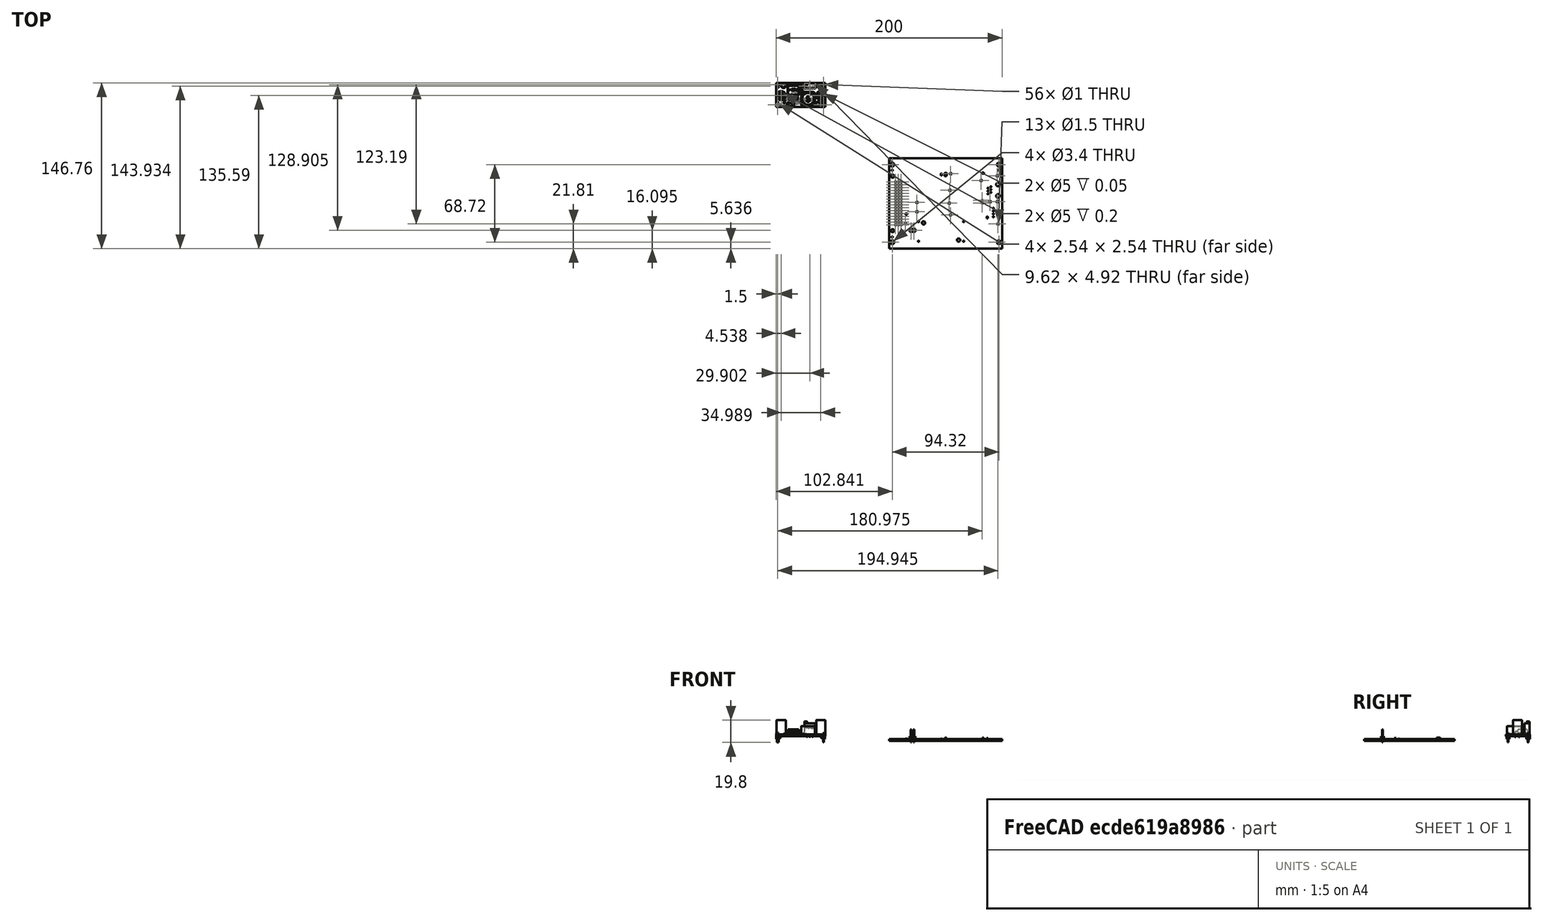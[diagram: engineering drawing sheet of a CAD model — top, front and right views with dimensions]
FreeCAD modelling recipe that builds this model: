
FCSTD DOCUMENT  (FreeCAD 0.19R24291 (Git))
Label: PolyVent_SPI_Controller_FreeCAD
License: All rights reserved
LicenseURL: http://en.wikipedia.org/wiki/All_rights_reserved
objects: Part::Feature×93, App::Link×56, App::Part×6, PartDesign::CoordinateSystem×1, Sketcher::SketchObject×1
note: 95 computed .brp shape members not serialized (recipe doc carries the construction recipe); baked Part::Feature solids carry a one-line shape summary decoded from their .brp

FEATURE [PartDesign::CoordinateSystem] Local_CS_b92b
  AttacherType = Attacher::AttachEngine3D
FEATURE [Part::Feature] Pcb_b92b
  shape: bbox 100 x 80 x 1.6 mm, 103 faces (baked)
FEATURE [Sketcher::SketchObject] PCB_Sketch_b92b
  FullyConstrained = false
  sketch-geometry (4):
    g0: LineSegment StartX=198.501 StartY=-145.004 StartZ=0 EndX=198.501 EndY=-65.0036 EndZ=0
    g1: LineSegment StartX=98.5011 StartY=-65.0036 StartZ=0 EndX=98.5011 EndY=-145.004 EndZ=0
    g2: LineSegment StartX=98.5011 StartY=-145.004 StartZ=0 EndX=198.501 EndY=-145.004 EndZ=0
    g3: LineSegment StartX=198.501 StartY=-65.0036 StartZ=0 EndX=98.5011 EndY=-65.0036 EndZ=0
  constraints (4):
    c: Coincident(g1,g2)
    c: Coincident(g1,g3)
    c: Coincident(g0,g2)
    c: Coincident(g0,g3)
FEATURE [App::Part] Board_Geoms_b92b
  Group = -> [Local_CS_b92b,Pcb_b92b,PCB_Sketch_b92b]
  Origin = -> Origin
FEATURE [Part::Feature] Shape  label="R113_R_0603_1608Metric_375481a100d2"
  Placement = pos=(144.78,-79.375,0) rot=(0,0,-1;1.5708rad)
  shape: bbox 0.8 x 1.6 x 0.45 mm, 26 faces (baked)
FEATURE [Part::Feature] Shape001  label="F103_Fuse_0603_1608Metric_acc948c9a6c3"
  Placement = pos=(113.817,-114.3,0) rot=(0,0,1;0rad)
  shape: bbox 1.6 x 0.8 x 0.45 mm, 26 faces (baked)
FEATURE [Part::Feature] Part__Feature  label="TestPoint_Loop_D2_54mm_Drill1_5mm_Beaded_cp"
  shape: bbox 3 x 3 x 3 mm, 4 faces (baked)
FEATURE [Part::Feature] Part__Feature001  label="TestPoint_Loop_D2_54mm_Drill1_5mm_Beaded_cp001"
  shape: bbox 3.415 x 0.9501 x 9.255 mm, 7 faces (baked)
FEATURE [App::Part] TestPoint_Loop_D2_54mm_Drill1_5mm_Beaded_cp  label="TP101_TestPoint_Loop_D2_54mm_Drill1_5mm_Beaded_cp002_d4c60d019c71"
  Group = -> [Part__Feature,Part__Feature001]
  Origin = -> Origin008
  Placement = pos=(180,-84.7725,0) rot=(0,0,1;0rad)
FEATURE [App::Link] R113_R_0603_1608Metric_375481a100d2_ln_  label="R107_R_0603_1608Metric_76be1ec9b680"
  LinkPlacement = pos=(147.678,-118.11,0) rot=(0,0,1;3.14159rad)
  LinkedObject = -> Shape
  Placement = pos=(147.678,-118.11,0) rot=(0,0,1;3.14159rad)
FEATURE [App::Link] R113_R_0603_1608Metric_375481a100d2_ln_001  label="R205_R_0603_1608Metric_6ebf565c5914"
  LinkPlacement = pos=(182.626,-111.76,0) rot=(0,0,1;3.14159rad)
  LinkedObject = -> Shape
  Placement = pos=(182.626,-111.76,0) rot=(0,0,1;3.14159rad)
FEATURE [App::Link] TP101_TestPoint_Loop_D2_54mm_Drill1_5mm_Beaded_cp002_d4c60d019c71_ln_  label="TP103_TestPoint_Loop_D2_54mm_Drill1_5mm_Beaded_cp002_1430d18448d9"
  LinkPlacement = pos=(152.4,-93.345,0) rot=(0,0,1;0rad)
  LinkedObject = -> TestPoint_Loop_D2_54mm_Drill1_5mm_Beaded_cp
  Placement = pos=(152.4,-93.345,0) rot=(0,0,1;0rad)
FEATURE [Part::Feature] Shape002  label="D101_LED_0603_1608Metric_bc9d04248380"
  Placement = pos=(181.61,-78.105,0) rot=(0,0,1;3.14159rad)
  shape: bbox 1.6 x 0.8 x 1.1 mm, 50 faces (baked)
FEATURE [App::Link] R113_R_0603_1608Metric_375481a100d2_ln_002  label="R102_R_0603_1608Metric_2d86cc6ea8c2"
  LinkPlacement = pos=(119.38,-133.35,0) rot=(0,0,1;0rad)
  LinkedObject = -> Shape
  Placement = pos=(119.38,-133.35,0) rot=(0,0,1;0rad)
FEATURE [App::Link] R113_R_0603_1608Metric_375481a100d2_ln_003  label="R111_R_0603_1608Metric_b8d57b534feb"
  LinkPlacement = pos=(144.145,-83.185,0) rot=(0,0,1;0rad)
  LinkedObject = -> Shape
  Placement = pos=(144.145,-83.185,0) rot=(0,0,1;0rad)
FEATURE [App::Link] R113_R_0603_1608Metric_375481a100d2_ln_004  label="R105_R_0603_1608Metric_261db71a386c"
  LinkPlacement = pos=(146.685,-109.22,0) rot=(0,0,1;3.14159rad)
  LinkedObject = -> Shape
  Placement = pos=(146.685,-109.22,0) rot=(0,0,1;3.14159rad)
FEATURE [App::Link] R113_R_0603_1608Metric_375481a100d2_ln_005  label="R117_R_0603_1608Metric_bc3712dd90b9"
  LinkPlacement = pos=(177.165,-78.105,0) rot=(0,0,1;3.14159rad)
  LinkedObject = -> Shape
  Placement = pos=(177.165,-78.105,0) rot=(0,0,1;3.14159rad)
FEATURE [App::Link] TP101_TestPoint_Loop_D2_54mm_Drill1_5mm_Beaded_cp002_d4c60d019c71_ln_001  label="TP106_TestPoint_Loop_D2_54mm_Drill1_5mm_Beaded_cp002_896a11763af9"
  LinkPlacement = pos=(123.19,-104.14,0) rot=(0,0,1;0rad)
  LinkedObject = -> TestPoint_Loop_D2_54mm_Drill1_5mm_Beaded_cp
  Placement = pos=(123.19,-104.14,0) rot=(0,0,1;0rad)
FEATURE [Part::Feature] Shape003  label="C202_C_0603_1608Metric_93a6a18d32bc"
  Placement = pos=(185.42,-117.475,0) rot=(0,0,-1;1.5708rad)
  shape: bbox 0.8 x 1.6 x 0.8 mm, 28 faces (baked)
FEATURE [App::Link] R113_R_0603_1608Metric_375481a100d2_ln_006  label="R108_R_0603_1608Metric_d8c6bf93a453"
  LinkPlacement = pos=(153.67,-83.185,0) rot=(0,0,1;3.14159rad)
  LinkedObject = -> Shape
  Placement = pos=(153.67,-83.185,0) rot=(0,0,1;3.14159rad)
FEATURE [App::Link] TP101_TestPoint_Loop_D2_54mm_Drill1_5mm_Beaded_cp002_d4c60d019c71_ln_002  label="TP203_TestPoint_Loop_D2_54mm_Drill1_5mm_Beaded_cp002_adb0e327fc1a"
  LinkPlacement = pos=(194.945,-123.19,0) rot=(0,0,1;0rad)
  LinkedObject = -> TestPoint_Loop_D2_54mm_Drill1_5mm_Beaded_cp
  Placement = pos=(194.945,-123.19,0) rot=(0,0,1;0rad)
FEATURE [App::Link] R113_R_0603_1608Metric_375481a100d2_ln_007  label="R103_R_0603_1608Metric_aa3dbe28ece3"
  LinkPlacement = pos=(148.59,-83.185,0) rot=(0,0,1;3.14159rad)
  LinkedObject = -> Shape
  Placement = pos=(148.59,-83.185,0) rot=(0,0,1;3.14159rad)
FEATURE [Part::Feature] Shape004  label="Q102_SOT_23_961175d790bb"
  Placement = pos=(148.59,-79.375,0) rot=(0,0,1;0rad)
  shape: bbox 2.5 x 3 x 1.2 mm, 76 faces (baked)
FEATURE [App::Link] R113_R_0603_1608Metric_375481a100d2_ln_008  label="R204_R_0603_1608Metric_f0bce681a641"
  LinkPlacement = pos=(176.53,-118.745,0) rot=(0,0,-1;1.5708rad)
  LinkedObject = -> Shape
  Placement = pos=(176.53,-118.745,0) rot=(0,0,-1;1.5708rad)
FEATURE [App::Link] TP101_TestPoint_Loop_D2_54mm_Drill1_5mm_Beaded_cp002_d4c60d019c71_ln_003  label="TP104_TestPoint_Loop_D2_54mm_Drill1_5mm_Beaded_cp002_f717344a846b"
  LinkPlacement = pos=(151.765,-104.775,0) rot=(0,0,1;0rad)
  LinkedObject = -> TestPoint_Loop_D2_54mm_Drill1_5mm_Beaded_cp
  Placement = pos=(151.765,-104.775,0) rot=(0,0,1;0rad)
FEATURE [App::Link] F103_Fuse_0603_1608Metric_acc948c9a6c3_ln_  label="F102_Fuse_0603_1608Metric_7bb2757e1e60"
  LinkPlacement = pos=(113.03,-108.585,0) rot=(0,0,1;0rad)
  LinkedObject = -> Shape001
  Placement = pos=(113.03,-108.585,0) rot=(0,0,1;0rad)
FEATURE [App::Link] R113_R_0603_1608Metric_375481a100d2_ln_009  label="R119_R_0603_1608Metric_ae8b03bb0e11"
  LinkPlacement = pos=(177.165,-71.755,0) rot=(0,0,1;3.14159rad)
  LinkedObject = -> Shape
  Placement = pos=(177.165,-71.755,0) rot=(0,0,1;3.14159rad)
FEATURE [App::Link] TP101_TestPoint_Loop_D2_54mm_Drill1_5mm_Beaded_cp002_d4c60d019c71_ln_004  label="TP105_TestPoint_Loop_D2_54mm_Drill1_5mm_Beaded_cp002_4d06bf4e9f5d"
  LinkPlacement = pos=(152.908,-115.189,0) rot=(0,0,1;0rad)
  LinkedObject = -> TestPoint_Loop_D2_54mm_Drill1_5mm_Beaded_cp
  Placement = pos=(152.908,-115.189,0) rot=(0,0,1;0rad)
FEATURE [App::Link] F103_Fuse_0603_1608Metric_acc948c9a6c3_ln_001  label="F101_Fuse_0603_1608Metric_b91510a6965f"
  LinkPlacement = pos=(114.3,-106.172,0) rot=(0,0,1;0rad)
  LinkedObject = -> Shape001
  Placement = pos=(114.3,-106.172,0) rot=(0,0,1;0rad)
FEATURE [Part::Feature] Shape005  label="J103_PinHeader_1x02_P254mm_Vertical_fd8e6863d4cd"
  Placement = pos=(118.11,-128.905,0) rot=(0,0,1;1.5708rad)
  shape: bbox 5.08 x 2.54 x 11.54 mm, 52 faces (baked)
FEATURE [App::Link] R113_R_0603_1608Metric_375481a100d2_ln_010  label="R114_R_0603_1608Metric_e7c9e8ab7085"
  LinkPlacement = pos=(144.145,-86.36,0) rot=(0,0,1;0rad)
  LinkedObject = -> Shape
  Placement = pos=(144.145,-86.36,0) rot=(0,0,1;0rad)
FEATURE [App::Link] R113_R_0603_1608Metric_375481a100d2_ln_011  label="R201_R_0603_1608Metric_d63957c1e1e8"
  LinkPlacement = pos=(167.64,-109.855,0) rot=(0,0,-1;1.5708rad)
  LinkedObject = -> Shape
  Placement = pos=(167.64,-109.855,0) rot=(0,0,-1;1.5708rad)
FEATURE [App::Link] R113_R_0603_1608Metric_375481a100d2_ln_012  label="R203_R_0603_1608Metric_9a6c50fd89f4"
  LinkPlacement = pos=(175.895,-109.22,0) rot=(0,0,-1;1.5708rad)
  LinkedObject = -> Shape
  Placement = pos=(175.895,-109.22,0) rot=(0,0,-1;1.5708rad)
FEATURE [App::Link] TP101_TestPoint_Loop_D2_54mm_Drill1_5mm_Beaded_cp002_d4c60d019c71_ln_005  label="TP108_TestPoint_Loop_D2_54mm_Drill1_5mm_Beaded_cp002_ea893a1c1d37"
  LinkPlacement = pos=(194.31,-80.645,0) rot=(0,0,1;0rad)
  LinkedObject = -> TestPoint_Loop_D2_54mm_Drill1_5mm_Beaded_cp
  Placement = pos=(194.31,-80.645,0) rot=(0,0,1;0rad)
FEATURE [App::Link] R113_R_0603_1608Metric_375481a100d2_ln_013  label="R118_R_0603_1608Metric_590b329d5cd8"
  LinkPlacement = pos=(177.442,-74.93,0) rot=(0,0,1;3.14159rad)
  LinkedObject = -> Shape
  Placement = pos=(177.442,-74.93,0) rot=(0,0,1;3.14159rad)
FEATURE [App::Link] R113_R_0603_1608Metric_375481a100d2_ln_014  label="R104_R_0603_1608Metric_1d251adcfbe1"
  LinkPlacement = pos=(147.678,-97.79,0) rot=(0,0,1;3.14159rad)
  LinkedObject = -> Shape
  Placement = pos=(147.678,-97.79,0) rot=(0,0,1;3.14159rad)
FEATURE [Part::Feature] Part__Feature002  label="YAAJ_DCDC_StepDown_LM2596_PinHeaders_cp"
  shape: bbox 2.54 x 2.541 x 8.5 mm, 105 faces (baked)
FEATURE [Part::Feature] Part__Feature003  label="YAAJ_DCDC_StepDown_LM2596_PinHeaders_cp001"
  shape: bbox 43.6 x 21.3 x 1.602 mm, 599 faces (baked)
FEATURE [Part::Feature] Part__Feature004  label="YAAJ_DCDC_StepDown_LM2596_PinHeaders_cp002"
  shape: bbox 2.19 x 2.19 x 1.52 mm, 24 faces (baked)
FEATURE [Part::Feature] Part__Feature005  label="YAAJ_DCDC_StepDown_LM2596_PinHeaders_cp003"
  shape: bbox 9.53 x 4.83 x 12.15 mm, 178 faces (baked)
FEATURE [Part::Feature] Part__Feature006  label="YAAJ_DCDC_StepDown_LM2596_PinHeaders_cp004"
  shape: bbox 9.92 x 5.22 x 0.001 mm, 10 faces (baked)
FEATURE [Part::Feature] Part__Feature007  label="YAAJ_DCDC_StepDown_LM2596_PinHeaders_cp005"
  shape: bbox 0.84 x 4.63 x 3.17 mm, 14 faces (baked)
FEATURE [Part::Feature] Part__Feature008  label="YAAJ_DCDC_StepDown_LM2596_PinHeaders_cp006"
  shape: bbox 0.84 x 4.63 x 3.17 mm, 14 faces (baked)
FEATURE [Part::Feature] Part__Feature009  label="YAAJ_DCDC_StepDown_LM2596_PinHeaders_cp007"
  shape: bbox 0.84 x 4.63 x 3.17 mm, 14 faces (baked)
FEATURE [Part::Feature] Part__Feature010  label="YAAJ_DCDC_StepDown_LM2596_PinHeaders_cp008"
  shape: bbox 0.84 x 4.63 x 3.17 mm, 14 faces (baked)
FEATURE [Part::Feature] Part__Feature011  label="YAAJ_DCDC_StepDown_LM2596_PinHeaders_cp009"
  shape: bbox 0.84 x 4.63 x 3.17 mm, 14 faces (baked)
FEATURE [Part::Feature] Part__Feature012  label="YAAJ_DCDC_StepDown_LM2596_PinHeaders_cp010"
  shape: bbox 10.16 x 9.72 x 4.571 mm, 273 faces (baked)
FEATURE [Part::Feature] Part__Feature013  label="YAAJ_DCDC_StepDown_LM2596_PinHeaders_cp011"
  shape: bbox 0.8 x 1.56 x 0.14 mm, 10 faces (baked)
FEATURE [Part::Feature] Part__Feature014  label="YAAJ_DCDC_StepDown_LM2596_PinHeaders_cp012"
  shape: bbox 0.05 x 0.07692 x 0.001 mm, 17 faces (baked)
FEATURE [Part::Feature] Part__Feature015  label="YAAJ_DCDC_StepDown_LM2596_PinHeaders_cp013"
  shape: bbox 0.05096 x 0.07885 x 0.001 mm, 12 faces (baked)
FEATURE [Part::Feature] Part__Feature016  label="YAAJ_DCDC_StepDown_LM2596_PinHeaders_cp014"
  shape: bbox 0.05096 x 0.07885 x 0.001 mm, 18 faces (baked)
FEATURE [Part::Feature] Part__Feature017  label="YAAJ_DCDC_StepDown_LM2596_PinHeaders_cp015"
  shape: bbox 1.61 x 1.062 x 0.001 mm, 10 faces (baked)
FEATURE [Part::Feature] Part__Feature018  label="YAAJ_DCDC_StepDown_LM2596_PinHeaders_cp016"
  shape: bbox 1.61 x 1.062 x 0.001 mm, 10 faces (baked)
FEATURE [Part::Feature] Part__Feature019  label="YAAJ_DCDC_StepDown_LM2596_PinHeaders_cp017"
  shape: bbox 0.001 x 0.03782 x 0.05 mm, 11 faces (baked)
FEATURE [Part::Feature] Part__Feature020  label="YAAJ_DCDC_StepDown_LM2596_PinHeaders_cp018"
  shape: bbox 0.001 x 0.05128 x 0.05256 mm, 29 faces (baked)
FEATURE [Part::Feature] Part__Feature021  label="YAAJ_DCDC_StepDown_LM2596_PinHeaders_cp019"
  shape: bbox 0.001 x 0.05128 x 0.05256 mm, 29 faces (baked)
FEATURE [Part::Feature] Part__Feature022  label="YAAJ_DCDC_StepDown_LM2596_PinHeaders_cp020"
  shape: bbox 0.001 x 0.02564 x 0.05128 mm, 10 faces (baked)
FEATURE [Part::Feature] Part__Feature023  label="YAAJ_DCDC_StepDown_LM2596_PinHeaders_cp021"
  shape: bbox 0.8 x 0.32 x 0.18 mm, 14 faces (baked)
FEATURE [Part::Feature] Part__Feature024  label="YAAJ_DCDC_StepDown_LM2596_PinHeaders_cp022"
  shape: bbox 0.05096 x 0.07885 x 0.001 mm, 12 faces (baked)
FEATURE [Part::Feature] Part__Feature025  label="YAAJ_DCDC_StepDown_LM2596_PinHeaders_cp023"
  shape: bbox 0.8 x 0.96 x 0.44 mm, 10 faces (baked)
FEATURE [Part::Feature] Part__Feature026  label="YAAJ_DCDC_StepDown_LM2596_PinHeaders_cp024"
  shape: bbox 0.8 x 0.32 x 0.181 mm, 16 faces (baked)
FEATURE [Part::Feature] Part__Feature027  label="YAAJ_DCDC_StepDown_LM2596_PinHeaders_cp025"
  shape: bbox 0.8 x 1.56 x 0.4 mm, 8 faces (baked)
FEATURE [Part::Feature] Part__Feature028  label="YAAJ_DCDC_StepDown_LM2596_PinHeaders_cp026"
  shape: bbox 0.1051 x 0.06795 x 0.001 mm, 18 faces (baked)
FEATURE [Part::Feature] Part__Feature029  label="YAAJ_DCDC_StepDown_LM2596_PinHeaders_cp027"
  shape: bbox 0.1051 x 0.06795 x 0.001 mm, 12 faces (baked)
FEATURE [Part::Feature] Part__Feature030  label="YAAJ_DCDC_StepDown_LM2596_PinHeaders_cp028"
  shape: bbox 0.1051 x 0.06154 x 0.001 mm, 13 faces (baked)
FEATURE [Part::Feature] Part__Feature031  label="YAAJ_DCDC_StepDown_LM2596_PinHeaders_cp029"
  shape: bbox 0.1051 x 0.06795 x 0.001 mm, 12 faces (baked)
FEATURE [Part::Feature] Part__Feature032  label="YAAJ_DCDC_StepDown_LM2596_PinHeaders_cp030"
  shape: bbox 1.61 x 1.195 x 0.001 mm, 10 faces (baked)
FEATURE [Part::Feature] Part__Feature033  label="YAAJ_DCDC_StepDown_LM2596_PinHeaders_cp031"
  shape: bbox 1.61 x 1.195 x 0.001 mm, 10 faces (baked)
FEATURE [Part::Feature] Part__Feature034  label="YAAJ_DCDC_StepDown_LM2596_PinHeaders_cp032"
  shape: bbox 0.001 x 0.03782 x 0.05 mm, 11 faces (baked)
FEATURE [Part::Feature] Part__Feature035  label="YAAJ_DCDC_StepDown_LM2596_PinHeaders_cp033"
  shape: bbox 0.001 x 0.05128 x 0.05256 mm, 29 faces (baked)
FEATURE [Part::Feature] Part__Feature036  label="YAAJ_DCDC_StepDown_LM2596_PinHeaders_cp034"
  shape: bbox 0.001 x 0.05128 x 0.05256 mm, 29 faces (baked)
FEATURE [Part::Feature] Part__Feature037  label="YAAJ_DCDC_StepDown_LM2596_PinHeaders_cp035"
  shape: bbox 0.001 x 0.02564 x 0.05128 mm, 10 faces (baked)
FEATURE [Part::Feature] Part__Feature038  label="YAAJ_DCDC_StepDown_LM2596_PinHeaders_cp036"
  shape: bbox 0.8 x 1.56 x 0.05 mm, 8 faces (baked)
FEATURE [Part::Feature] Part__Feature039  label="YAAJ_DCDC_StepDown_LM2596_PinHeaders_cp037"
  shape: bbox 0.8 x 0.32 x 0.49 mm, 14 faces (baked)
FEATURE [Part::Feature] Part__Feature040  label="YAAJ_DCDC_StepDown_LM2596_PinHeaders_cp038"
  shape: bbox 0.8 x 0.32 x 0.49 mm, 14 faces (baked)
FEATURE [Part::Feature] Part__Feature041  label="YAAJ_DCDC_StepDown_LM2596_PinHeaders_cp039"
  shape: bbox 0.8 x 1.56 x 0.4 mm, 8 faces (baked)
FEATURE [Part::Feature] Part__Feature042  label="YAAJ_DCDC_StepDown_LM2596_PinHeaders_cp040"
  shape: bbox 0.1051 x 0.06795 x 0.001 mm, 18 faces (baked)
FEATURE [Part::Feature] Part__Feature043  label="YAAJ_DCDC_StepDown_LM2596_PinHeaders_cp041"
  shape: bbox 0.1051 x 0.06795 x 0.001 mm, 12 faces (baked)
FEATURE [Part::Feature] Part__Feature044  label="YAAJ_DCDC_StepDown_LM2596_PinHeaders_cp042"
  shape: bbox 0.1051 x 0.06154 x 0.001 mm, 13 faces (baked)
FEATURE [Part::Feature] Part__Feature045  label="YAAJ_DCDC_StepDown_LM2596_PinHeaders_cp043"
  shape: bbox 0.1051 x 0.06795 x 0.001 mm, 12 faces (baked)
FEATURE [Part::Feature] Part__Feature046  label="YAAJ_DCDC_StepDown_LM2596_PinHeaders_cp044"
  shape: bbox 1.61 x 1.195 x 0.001 mm, 10 faces (baked)
FEATURE [Part::Feature] Part__Feature047  label="YAAJ_DCDC_StepDown_LM2596_PinHeaders_cp045"
  shape: bbox 1.61 x 1.195 x 0.001 mm, 10 faces (baked)
FEATURE [Part::Feature] Part__Feature048  label="YAAJ_DCDC_StepDown_LM2596_PinHeaders_cp046"
  shape: bbox 0.001 x 0.03782 x 0.05 mm, 11 faces (baked)
FEATURE [Part::Feature] Part__Feature049  label="YAAJ_DCDC_StepDown_LM2596_PinHeaders_cp047"
  shape: bbox 0.001 x 0.05128 x 0.05256 mm, 29 faces (baked)
FEATURE [Part::Feature] Part__Feature050  label="YAAJ_DCDC_StepDown_LM2596_PinHeaders_cp048"
  shape: bbox 0.001 x 0.05128 x 0.05256 mm, 29 faces (baked)
FEATURE [Part::Feature] Part__Feature051  label="YAAJ_DCDC_StepDown_LM2596_PinHeaders_cp049"
  shape: bbox 0.001 x 0.02564 x 0.05128 mm, 10 faces (baked)
FEATURE [Part::Feature] Part__Feature052  label="YAAJ_DCDC_StepDown_LM2596_PinHeaders_cp050"
  shape: bbox 0.8 x 1.56 x 0.05 mm, 8 faces (baked)
FEATURE [Part::Feature] Part__Feature053  label="YAAJ_DCDC_StepDown_LM2596_PinHeaders_cp051"
  shape: bbox 0.8 x 0.32 x 0.49 mm, 14 faces (baked)
FEATURE [Part::Feature] Part__Feature054  label="YAAJ_DCDC_StepDown_LM2596_PinHeaders_cp052"
  shape: bbox 0.8 x 0.32 x 0.49 mm, 14 faces (baked)
FEATURE [Part::Feature] Part__Feature055  label="YAAJ_DCDC_StepDown_LM2596_PinHeaders_cp053"
  shape: bbox 0.1051 x 0.06795 x 0.001 mm, 18 faces (baked)
FEATURE [Part::Feature] Part__Feature056  label="YAAJ_DCDC_StepDown_LM2596_PinHeaders_cp054"
  shape: bbox 0.1051 x 0.06795 x 0.001 mm, 12 faces (baked)
FEATURE [Part::Feature] Part__Feature057  label="YAAJ_DCDC_StepDown_LM2596_PinHeaders_cp055"
  shape: bbox 0.1051 x 0.06154 x 0.001 mm, 13 faces (baked)
FEATURE [Part::Feature] Part__Feature058  label="YAAJ_DCDC_StepDown_LM2596_PinHeaders_cp056"
  shape: bbox 0.1051 x 0.06795 x 0.001 mm, 12 faces (baked)
FEATURE [Part::Feature] Part__Feature059  label="YAAJ_DCDC_StepDown_LM2596_PinHeaders_cp057"
  shape: bbox 1.61 x 1.062 x 0.001 mm, 10 faces (baked)
FEATURE [Part::Feature] Part__Feature060  label="YAAJ_DCDC_StepDown_LM2596_PinHeaders_cp058"
  shape: bbox 1.61 x 1.062 x 0.001 mm, 10 faces (baked)
FEATURE [Part::Feature] Part__Feature061  label="YAAJ_DCDC_StepDown_LM2596_PinHeaders_cp059"
  shape: bbox 0.001 x 0.03782 x 0.05 mm, 11 faces (baked)
FEATURE [Part::Feature] Part__Feature062  label="YAAJ_DCDC_StepDown_LM2596_PinHeaders_cp060"
  shape: bbox 0.001 x 0.05128 x 0.05256 mm, 29 faces (baked)
FEATURE [Part::Feature] Part__Feature063  label="YAAJ_DCDC_StepDown_LM2596_PinHeaders_cp061"
  shape: bbox 0.001 x 0.05128 x 0.05256 mm, 29 faces (baked)
FEATURE [Part::Feature] Part__Feature064  label="YAAJ_DCDC_StepDown_LM2596_PinHeaders_cp062"
  shape: bbox 0.001 x 0.02564 x 0.05128 mm, 10 faces (baked)
FEATURE [Part::Feature] Part__Feature065  label="YAAJ_DCDC_StepDown_LM2596_PinHeaders_cp063"
  shape: bbox 0.8 x 1.6 x 0.74 mm, 44 faces (baked)
FEATURE [Part::Feature] Part__Feature066  label="YAAJ_DCDC_StepDown_LM2596_PinHeaders_cp064"
  shape: bbox 2.175 x 3.15 x 0.001 mm, 10 faces (baked)
FEATURE [Part::Feature] Part__Feature067  label="YAAJ_DCDC_StepDown_LM2596_PinHeaders_cp065"
  shape: bbox 2.175 x 3.15 x 0.001 mm, 10 faces (baked)
FEATURE [Part::Feature] Part__Feature068  label="YAAJ_DCDC_StepDown_LM2596_PinHeaders_cp066"
  shape: bbox 4.7 x 2.5 x 1.101 mm, 199 faces (baked)
FEATURE [Part::Feature] Part__Feature069  label="YAAJ_DCDC_StepDown_LM2596_PinHeaders_cp067"
  shape: bbox 0.1051 x 0.06795 x 0.001 mm, 18 faces (baked)
FEATURE [Part::Feature] Part__Feature070  label="YAAJ_DCDC_StepDown_LM2596_PinHeaders_cp068"
  shape: bbox 0.1051 x 0.06795 x 0.001 mm, 12 faces (baked)
FEATURE [Part::Feature] Part__Feature071  label="YAAJ_DCDC_StepDown_LM2596_PinHeaders_cp069"
  shape: bbox 0.1051 x 0.06154 x 0.001 mm, 13 faces (baked)
FEATURE [Part::Feature] Part__Feature072  label="YAAJ_DCDC_StepDown_LM2596_PinHeaders_cp070"
  shape: bbox 0.1051 x 0.06795 x 0.001 mm, 12 faces (baked)
FEATURE [Part::Feature] Part__Feature073  label="YAAJ_DCDC_StepDown_LM2596_PinHeaders_cp071"
  shape: bbox 1.61 x 1.062 x 0.001 mm, 10 faces (baked)
FEATURE [Part::Feature] Part__Feature074  label="YAAJ_DCDC_StepDown_LM2596_PinHeaders_cp072"
  shape: bbox 1.61 x 1.062 x 0.001 mm, 10 faces (baked)
FEATURE [Part::Feature] Part__Feature075  label="YAAJ_DCDC_StepDown_LM2596_PinHeaders_cp073"
  shape: bbox 0.001 x 0.03782 x 0.05 mm, 11 faces (baked)
FEATURE [Part::Feature] Part__Feature076  label="YAAJ_DCDC_StepDown_LM2596_PinHeaders_cp074"
  shape: bbox 0.001 x 0.05128 x 0.05256 mm, 29 faces (baked)
FEATURE [Part::Feature] Part__Feature077  label="YAAJ_DCDC_StepDown_LM2596_PinHeaders_cp075"
  shape: bbox 0.001 x 0.05128 x 0.05256 mm, 29 faces (baked)
FEATURE [Part::Feature] Part__Feature078  label="YAAJ_DCDC_StepDown_LM2596_PinHeaders_cp076"
  shape: bbox 0.001 x 0.02564 x 0.05128 mm, 10 faces (baked)
FEATURE [Part::Feature] Part__Feature079  label="YAAJ_DCDC_StepDown_LM2596_PinHeaders_cp077"
  shape: bbox 0.8 x 1.6 x 0.74 mm, 44 faces (baked)
FEATURE [Part::Feature] Part__Feature080  label="YAAJ_DCDC_StepDown_LM2596_PinHeaders_cp078"
  shape: bbox 12.82 x 12.82 x 7.301 mm, 156 faces (baked)
FEATURE [Part::Feature] Part__Feature081  label="YAAJ_DCDC_StepDown_LM2596_PinHeaders_cp079"
  shape: bbox 8.659 x 8.659 x 15.15 mm, 75 faces (baked)
FEATURE [Part::Feature] Part__Feature082  label="YAAJ_DCDC_StepDown_LM2596_PinHeaders_cp080"
  shape: bbox 8.659 x 8.659 x 15.15 mm, 75 faces (baked)
FEATURE [Part::Feature] Part__Feature083  label="YAAJ_DCDC_StepDown_LM2596_PinHeaders_cp081"
  shape: bbox 2.54 x 2.541 x 8.5 mm, 105 faces (baked)
FEATURE [Part::Feature] Part__Feature084  label="YAAJ_DCDC_StepDown_LM2596_PinHeaders_cp082"
  shape: bbox 2.54 x 2.541 x 8.5 mm, 105 faces (baked)
FEATURE [Part::Feature] Part__Feature085  label="YAAJ_DCDC_StepDown_LM2596_PinHeaders_cp083"
  shape: bbox 2.54 x 2.541 x 8.5 mm, 105 faces (baked)
FEATURE [App::Part] YAAJ_DCDC_StepDown_LM2596_PinHeaders_cp  label="U101_YAAJ_DCDC_StepDown_LM2596_PinHeaders_cp084_858511852adb"
  Group = -> [Part__Feature002,Part__Feature003,Part__Feature004,Part__Feature005,Part__Feature006,Part__Feature007,Part__Feature008,Part__Feature009,Part__Feature010,Part__Feature011,Part__Feature012,Part__Feature013,Part__Feature014,Part__Feature015,Part__Feature016,Part__Feature017,Part__Feature018,Part__Feature019,Part__Feature020,Part__Feature021,Part__Feature022,Part__Feature023,Part__Feature024,+61 more]
  Origin = -> Origin009
  Placement = pos=(124.841,-121.285,0) rot=(0,0,1;0rad)
FEATURE [App::Link] TP101_TestPoint_Loop_D2_54mm_Drill1_5mm_Beaded_cp002_d4c60d019c71_ln_006  label="TP201_TestPoint_Loop_D2_54mm_Drill1_5mm_Beaded_cp002_b67a7eb8728f"
  LinkPlacement = pos=(194.31,-103.505,0) rot=(0,0,1;0rad)
  LinkedObject = -> TestPoint_Loop_D2_54mm_Drill1_5mm_Beaded_cp
  Placement = pos=(194.31,-103.505,0) rot=(0,0,1;0rad)
FEATURE [App::Link] Q102_SOT_23_961175d790bb_ln_  label="Q104_SOT_23_e511b557bddc"
  LinkPlacement = pos=(146.685,-104.775,0) rot=(0,0,1;0rad)
  LinkedObject = -> Shape004
  Placement = pos=(146.685,-104.775,0) rot=(0,0,1;0rad)
FEATURE [App::Link] TP101_TestPoint_Loop_D2_54mm_Drill1_5mm_Beaded_cp002_d4c60d019c71_ln_007  label="TP109_TestPoint_Loop_D2_54mm_Drill1_5mm_Beaded_cp002_d7b4b6b944ca"
  LinkPlacement = pos=(113.03,-123.19,0) rot=(0,0,1;0rad)
  LinkedObject = -> TestPoint_Loop_D2_54mm_Drill1_5mm_Beaded_cp
  Placement = pos=(113.03,-123.19,0) rot=(0,0,1;0rad)
FEATURE [App::Link] R113_R_0603_1608Metric_375481a100d2_ln_015  label="R106_R_0603_1608Metric_acca555762d5"
  LinkPlacement = pos=(151.638,-118.11,0) rot=(0,0,1;3.14159rad)
  LinkedObject = -> Shape
  Placement = pos=(151.638,-118.11,0) rot=(0,0,1;3.14159rad)
FEATURE [App::Link] C202_C_0603_1608Metric_93a6a18d32bc_ln_  label="C201_C_0603_1608Metric_d23be7bb3a10"
  LinkPlacement = pos=(185.42,-113.03,0) rot=(0,0,-1;1.5708rad)
  LinkedObject = -> Shape003
  Placement = pos=(185.42,-113.03,0) rot=(0,0,-1;1.5708rad)
FEATURE [App::Link] C202_C_0603_1608Metric_93a6a18d32bc_ln_001  label="C106_C_0603_1608Metric_e8e5381aa997"
  LinkPlacement = pos=(117.475,-109.855,0) rot=(0,0,-1;1.5708rad)
  LinkedObject = -> Shape003
  Placement = pos=(117.475,-109.855,0) rot=(0,0,-1;1.5708rad)
FEATURE [App::Link] Q102_SOT_23_961175d790bb_ln_001  label="Q103_SOT_23_589ad7ff1685"
  LinkPlacement = pos=(147.32,-93.98,0) rot=(0,0,1;0rad)
  LinkedObject = -> Shape004
  Placement = pos=(147.32,-93.98,0) rot=(0,0,1;0rad)
FEATURE [App::Link] TP101_TestPoint_Loop_D2_54mm_Drill1_5mm_Beaded_cp002_d4c60d019c71_ln_008  label="TP202_TestPoint_Loop_D2_54mm_Drill1_5mm_Beaded_cp002_bba5311270d3"
  LinkPlacement = pos=(187.96,-103.505,0) rot=(0,0,1;0rad)
  LinkedObject = -> TestPoint_Loop_D2_54mm_Drill1_5mm_Beaded_cp
  Placement = pos=(187.96,-103.505,0) rot=(0,0,1;0rad)
FEATURE [App::Link] C202_C_0603_1608Metric_93a6a18d32bc_ln_002  label="C103_C_0603_1608Metric_56500de4e25a"
  LinkPlacement = pos=(181.61,-97.155,0) rot=(0,0,-1;1.5708rad)
  LinkedObject = -> Shape003
  Placement = pos=(181.61,-97.155,0) rot=(0,0,-1;1.5708rad)
FEATURE [App::Link] R113_R_0603_1608Metric_375481a100d2_ln_016  label="R120_R_0603_1608Metric_c797d29c78d1"
  LinkPlacement = pos=(187.452,-126.746,0) rot=(0,0,1;3.14159rad)
  LinkedObject = -> Shape
  Placement = pos=(187.452,-126.746,0) rot=(0,0,1;3.14159rad)
FEATURE [App::Link] R113_R_0603_1608Metric_375481a100d2_ln_017  label="R207_R_0603_1608Metric_317c5b8d8895"
  LinkPlacement = pos=(173.99,-104.14,0) rot=(0,0,1;3.14159rad)
  LinkedObject = -> Shape
  Placement = pos=(173.99,-104.14,0) rot=(0,0,1;3.14159rad)
FEATURE [App::Link] R113_R_0603_1608Metric_375481a100d2_ln_018  label="R208_R_0603_1608Metric_29f8c7bf1ec5"
  LinkPlacement = pos=(173.99,-100.965,0) rot=(0,0,1;0rad)
  LinkedObject = -> Shape
  Placement = pos=(173.99,-100.965,0) rot=(0,0,1;0rad)
FEATURE [App::Link] R113_R_0603_1608Metric_375481a100d2_ln_019  label="R202_R_0603_1608Metric_245c83ed6b32"
  LinkPlacement = pos=(168.91,-120.015,0) rot=(0,0,-1;1.5708rad)
  LinkedObject = -> Shape
  Placement = pos=(168.91,-120.015,0) rot=(0,0,-1;1.5708rad)
FEATURE [App::Link] J103_PinHeader_1x02_P254mm_Vertical_fd8e6863d4cd_ln_  label="J202_PinHeader_1x02_P254mm_Vertical_f39f1a503d2a"
  LinkPlacement = pos=(180.975,-104.78,0) rot=(0,0,1;3.14159rad)
  LinkedObject = -> Shape005
  Placement = pos=(180.975,-104.78,0) rot=(0,0,1;3.14159rad)
FEATURE [App::Link] C202_C_0603_1608Metric_93a6a18d32bc_ln_003  label="C104_C_0603_1608Metric_578cfebcb37b"
  LinkPlacement = pos=(177.165,-100.33,0) rot=(0,0,-1;1.5708rad)
  LinkedObject = -> Shape003
  Placement = pos=(177.165,-100.33,0) rot=(0,0,-1;1.5708rad)
FEATURE [App::Link] C202_C_0603_1608Metric_93a6a18d32bc_ln_004  label="C105_C_0603_1608Metric_66f380e839ba"
  LinkPlacement = pos=(119.888,-105.664,0) rot=(0,0,-1;1.5708rad)
  LinkedObject = -> Shape003
  Placement = pos=(119.888,-105.664,0) rot=(0,0,-1;1.5708rad)
FEATURE [App::Link] C202_C_0603_1608Metric_93a6a18d32bc_ln_005  label="C107_C_0603_1608Metric_f7687f34a7a1"
  LinkPlacement = pos=(117.475,-116.205,0) rot=(0,0,-1;1.5708rad)
  LinkedObject = -> Shape003
  Placement = pos=(117.475,-116.205,0) rot=(0,0,-1;1.5708rad)
FEATURE [App::Link] R113_R_0603_1608Metric_375481a100d2_ln_020  label="R112_R_0603_1608Metric_62eeb006f087"
  LinkPlacement = pos=(144.018,-115.062,0) rot=(0,0,-1;1.5708rad)
  LinkedObject = -> Shape
  Placement = pos=(144.018,-115.062,0) rot=(0,0,-1;1.5708rad)
FEATURE [App::Link] R113_R_0603_1608Metric_375481a100d2_ln_021  label="R116_R_0603_1608Metric_8ddf04130333"
  LinkPlacement = pos=(142.875,-109.22,0) rot=(0,0,1;0rad)
  LinkedObject = -> Shape
  Placement = pos=(142.875,-109.22,0) rot=(0,0,1;0rad)
FEATURE [App::Link] C202_C_0603_1608Metric_93a6a18d32bc_ln_006  label="C101_C_0603_1608Metric_d56235c6cd45"
  LinkPlacement = pos=(181.61,-92.71,0) rot=(0,0,-1;1.5708rad)
  LinkedObject = -> Shape003
  Placement = pos=(181.61,-92.71,0) rot=(0,0,-1;1.5708rad)
FEATURE [App::Link] Q102_SOT_23_961175d790bb_ln_002  label="Q202_SOT_23_612fa1793d34"
  LinkPlacement = pos=(172.72,-120.015,0) rot=(0,0,1;0rad)
  LinkedObject = -> Shape004
  Placement = pos=(172.72,-120.015,0) rot=(0,0,1;0rad)
FEATURE [App::Link] R113_R_0603_1608Metric_375481a100d2_ln_022  label="R109_R_0603_1608Metric_c0cccce3f511"
  LinkPlacement = pos=(152.123,-97.79,0) rot=(0,0,1;3.14159rad)
  LinkedObject = -> Shape
  Placement = pos=(152.123,-97.79,0) rot=(0,0,1;3.14159rad)
FEATURE [App::Link] TP101_TestPoint_Loop_D2_54mm_Drill1_5mm_Beaded_cp002_d4c60d019c71_ln_009  label="TP107_TestPoint_Loop_D2_54mm_Drill1_5mm_Beaded_cp002_d0dc02f774c7"
  LinkPlacement = pos=(123.19,-112.395,0) rot=(0,0,1;0rad)
  LinkedObject = -> TestPoint_Loop_D2_54mm_Drill1_5mm_Beaded_cp
  Placement = pos=(123.19,-112.395,0) rot=(0,0,1;0rad)
FEATURE [App::Link] R113_R_0603_1608Metric_375481a100d2_ln_023  label="R206_R_0603_1608Metric_ed69066bbbdc"
  LinkPlacement = pos=(181.967,-116.84,0) rot=(0,0,1;3.14159rad)
  LinkedObject = -> Shape
  Placement = pos=(181.967,-116.84,0) rot=(0,0,1;3.14159rad)
FEATURE [App::Link] R113_R_0603_1608Metric_375481a100d2_ln_024  label="R101_R_0603_1608Metric_cf8e4b0844bd"
  LinkPlacement = pos=(117.475,-122.555,0) rot=(0,0,1;1.5708rad)
  LinkedObject = -> Shape
  Placement = pos=(117.475,-122.555,0) rot=(0,0,1;1.5708rad)
FEATURE [App::Link] D101_LED_0603_1608Metric_bc9d04248380_ln_  label="D102_LED_0603_1608Metric_73077cea72a4"
  LinkPlacement = pos=(181.61,-74.93,0) rot=(0,0,1;3.14159rad)
  LinkedObject = -> Shape002
  Placement = pos=(181.61,-74.93,0) rot=(0,0,1;3.14159rad)
FEATURE [App::Link] Q102_SOT_23_961175d790bb_ln_003  label="Q201_SOT_23_3297bb07adb6"
  LinkPlacement = pos=(172.085,-109.855,0) rot=(0,0,1;0rad)
  LinkedObject = -> Shape004
  Placement = pos=(172.085,-109.855,0) rot=(0,0,1;0rad)
FEATURE [App::Link] Q102_SOT_23_961175d790bb_ln_004  label="Q101_SOT_23_11f12e2cb1c3"
  LinkPlacement = pos=(147.703,-115.062,0) rot=(0,0,1;0rad)
  LinkedObject = -> Shape004
  Placement = pos=(147.703,-115.062,0) rot=(0,0,1;0rad)
FEATURE [App::Link] D101_LED_0603_1608Metric_bc9d04248380_ln_001  label="D103_LED_0603_1608Metric_9574bf049cba"
  LinkPlacement = pos=(181.61,-71.755,0) rot=(0,0,1;3.14159rad)
  LinkedObject = -> Shape002
  Placement = pos=(181.61,-71.755,0) rot=(0,0,1;3.14159rad)
FEATURE [App::Link] R113_R_0603_1608Metric_375481a100d2_ln_025  label="R115_R_0603_1608Metric_2e7e72ad4692"
  LinkPlacement = pos=(141.605,-95.25,0) rot=(0,0,-1;1.5708rad)
  LinkedObject = -> Shape
  Placement = pos=(141.605,-95.25,0) rot=(0,0,-1;1.5708rad)
FEATURE [App::Link] R113_R_0603_1608Metric_375481a100d2_ln_026  label="R110_R_0603_1608Metric_e8693063be8c"
  LinkPlacement = pos=(151.765,-109.22,0) rot=(0,0,1;3.14159rad)
  LinkedObject = -> Shape
  Placement = pos=(151.765,-109.22,0) rot=(0,0,1;3.14159rad)
FEATURE [App::Link] TP101_TestPoint_Loop_D2_54mm_Drill1_5mm_Beaded_cp002_d4c60d019c71_ln_010  label="TP102_TestPoint_Loop_D2_54mm_Drill1_5mm_Beaded_cp002_83b165b12e46"
  LinkPlacement = pos=(153.035,-78.74,0) rot=(0,0,1;0rad)
  LinkedObject = -> TestPoint_Loop_D2_54mm_Drill1_5mm_Beaded_cp
  Placement = pos=(153.035,-78.74,0) rot=(0,0,1;0rad)
FEATURE [App::Link] C202_C_0603_1608Metric_93a6a18d32bc_ln_007  label="C102_C_0603_1608Metric_1365fd17f38b"
  LinkPlacement = pos=(177.165,-95.25,0) rot=(0,0,-1;1.5708rad)
  LinkedObject = -> Shape003
  Placement = pos=(177.165,-95.25,0) rot=(0,0,-1;1.5708rad)
FEATURE [App::Part] Top_b92b
  Group = -> [Shape,Shape001,TestPoint_Loop_D2_54mm_Drill1_5mm_Beaded_cp,R113_R_0603_1608Metric_375481a100d2_ln_,R113_R_0603_1608Metric_375481a100d2_ln_001,TP101_TestPoint_Loop_D2_54mm_Drill1_5mm_Beaded_cp002_d4c60d019c71_ln_,Shape002,R113_R_0603_1608Metric_375481a100d2_ln_002,R113_R_0603_1608Metric_375481a100d2_ln_003,R113_R_0603_1608Metric_375481a100d2_ln_004,R113_R_0603_1608Metric_375481a100d2_ln_005,+53 more]
  Origin = -> Origin003
FEATURE [App::Part] Step_Models_b92b
  Group = -> [Top_b92b]
  Origin = -> Origin002
FEATURE [App::Part] Board_b92b  label="PolyVent_SPI_Controller"
  Group = -> [Board_Geoms_b92b,Step_Models_b92b]
  Origin = -> Origin001
